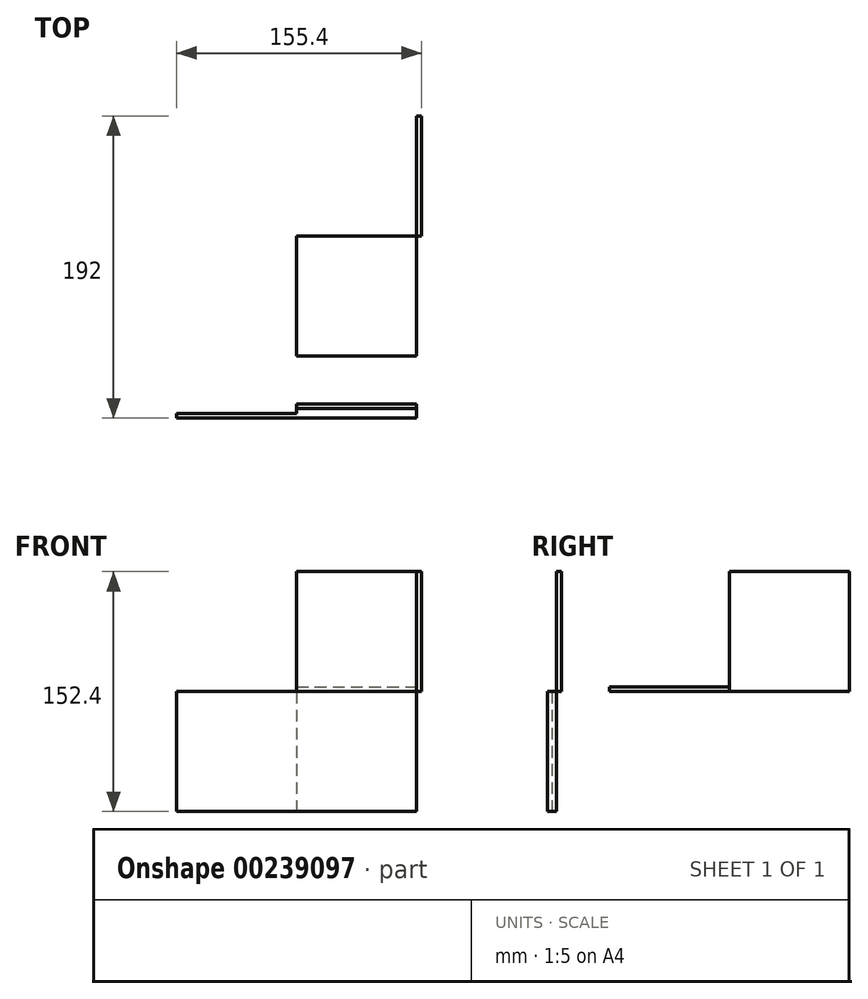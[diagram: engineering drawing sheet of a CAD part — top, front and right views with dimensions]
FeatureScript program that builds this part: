
annotation { "Feature Type Name" : "Feature", "Feature Type Description" : "" }
export const myFeature = defineFeature(function(context is Context, id is Id, definition is map)
    precondition{}
    {
        {
            assignVariable(context, id + "F0", {"name" : "v", "anyValue" : 3});
        }
        {
            var Q0;
            Q0=qCreatedBy(makeId("Front.planeOp"),FACE);
            var sketch = newSketch(context, id + "F1", { "sketchPlane" : qUnion([Q0])});
            skLineSegment(sketch, "E0.bottom", {"start": v(-76.2, 38.1) * mm, "end": v(76.2, 38.1) * mm});
            skLineSegment(sketch, "E0.top", {"start": v(-76.2, -38.1) * mm, "end": v(76.2, -38.1) * mm});
            skLineSegment(sketch, "E0.left", {"start": v(-76.2, 38.1) * mm, "end": v(-76.2, -38.1) * mm});
            skLineSegment(sketch, "E0.right", {"start": v(76.2, 38.1) * mm, "end": v(76.2, -38.1) * mm});
            skPoint(sketch, "E0.middle", {"position": v(0, 0) * mm});
            skSolve(sketch);
        }
        {
            var Q0;
            Q0 = qSketchRegion(id + "F1", true);
            extrude(context, id + "F2", {"entities" : qUnion([Q0]), "endBound" : BoundingType.SYMMETRIC, "depth" : (getVariable(context, 'v')) * mm});
        }
        {
            var Q0;
            Q0=makeQuery(id+"F2.opExtrude","CAP_FACE",FACE,{"disambiguationData":[OSD([sQuery(id+"F1.wireOp",EDGE,"E0.bottom"),sQuery(id+"F1.wireOp",EDGE,"E0.top"),sQuery(id+"F1.wireOp",EDGE,"E0.left"),sQuery(id+"F1.wireOp",EDGE,"E0.right")])],"isStart":true});
            var sketch = newSketch(context, id + "F3", { "sketchPlane" : qUnion([Q0])});
            skLineSegment(sketch, "E1.bottom", {"start": v(-76.2, 38.1) * mm, "end": v(0, 38.1) * mm});
            skLineSegment(sketch, "E1.top", {"start": v(-76.2, -38.1) * mm, "end": v(0, -38.1) * mm});
            skLineSegment(sketch, "E1.left", {"start": v(-76.2, 38.1) * mm, "end": v(-76.2, -38.1) * mm});
            skLineSegment(sketch, "E1.right", {"start": v(0, 38.1) * mm, "end": v(0, -38.1) * mm});
            skSolve(sketch);
        }
        {
            var Q0;
            Q0 = qSketchRegion(id + "F3", true);
            extrude(context, id + "F4", {"entities" : qUnion([Q0]), "operationType" : NewBodyOperationType.ADD, "depth" : (getVariable(context, 'v')) * mm});
        }
        {
            var Q0;
            Q0=makeQuery(id+"F4.boolean.opBoolean","MERGE",FACE,{"derivedFrom":[makeQuery(id+"F2.opExtrude","SWEPT_FACE",FACE,{"disambiguationData":[OSD([sQuery(id+"F1.wireOp",EDGE,"E0.bottom")])]}),makeQuery(id+"F4.opExtrude","SWEPT_FACE",FACE,{"disambiguationData":[OSD([sQuery(id+"F3.wireOp",EDGE,"E1.bottom")])]})]});
            var sketch = newSketch(context, id + "F5", { "sketchPlane" : qUnion([Q0])});
            skLineSegment(sketch, "E2.bottom", {"start": v(0, 114.3) * mm, "end": v(76.2, 114.3) * mm});
            skLineSegment(sketch, "E2.top", {"start": v(0, 38.1) * mm, "end": v(76.2, 38.1) * mm});
            skLineSegment(sketch, "E2.left", {"start": v(0, 114.3) * mm, "end": v(0, 38.1) * mm});
            skLineSegment(sketch, "E2.right", {"start": v(76.2, 114.3) * mm, "end": v(76.2, 38.1) * mm});
            skSolve(sketch);
        }
        {
            var Q0;
            Q0 = qSketchRegion(id + "F5", true);
            extrude(context, id + "F6", {"entities" : qUnion([Q0]), "operationType" : NewBodyOperationType.ADD, "depth" : (getVariable(context, 'v')) * mm});
        }
        {
            var Q0;
            Q0=makeQuery(id+"F6.boolean.opBoolean","MERGE",FACE,{"derivedFrom":[makeQuery(id+"F4.opExtrude","CAP_FACE",FACE,{"disambiguationData":[OSD([sQuery(id+"F3.wireOp",EDGE,"E1.bottom"),sQuery(id+"F3.wireOp",EDGE,"E1.top"),sQuery(id+"F3.wireOp",EDGE,"E1.left"),sQuery(id+"F3.wireOp",EDGE,"E1.right")])],"isStart":false}),makeQuery(id+"F6.opExtrude","SWEPT_FACE",FACE,{"disambiguationData":[OSD([sQuery(id+"F5.wireOp",EDGE,"E2.bottom")])]})]});
            var sketch = newSketch(context, id + "F7", { "sketchPlane" : qUnion([Q0])});
            skLineSegment(sketch, "E3.bottom", {"start": v(-76.2, 114.3) * mm, "end": v(0, 114.3) * mm});
            skLineSegment(sketch, "E3.top", {"start": v(-76.2, 38.1) * mm, "end": v(0, 38.1) * mm});
            skLineSegment(sketch, "E3.left", {"start": v(-76.2, 114.3) * mm, "end": v(-76.2, 38.1) * mm});
            skLineSegment(sketch, "E3.right", {"start": v(0, 114.3) * mm, "end": v(0, 38.1) * mm});
            skSolve(sketch);
        }
        {
            var Q0;
            Q0 = qSketchRegion(id + "F7", true);
            extrude(context, id + "F8", {"entities" : qUnion([Q0]), "operationType" : NewBodyOperationType.ADD, "depth" : (getVariable(context, 'v')) * mm});
        }
        {
            var Q0;
            Q0=makeQuery(id+"F8.boolean.opBoolean","MERGE",FACE,{"derivedFrom":[makeQuery(id+"F6.boolean.opBoolean","MERGE",FACE,{"derivedFrom":[makeQuery(id+"F4.boolean.opBoolean","MERGE",FACE,{"derivedFrom":[makeQuery(id+"F2.opExtrude","SWEPT_FACE",FACE,{"disambiguationData":[OSD([sQuery(id+"F1.wireOp",EDGE,"E0.right")])]}),makeQuery(id+"F4.opExtrude","SWEPT_FACE",FACE,{"disambiguationData":[OSD([sQuery(id+"F3.wireOp",EDGE,"E1.left")])]})]}),makeQuery(id+"F6.opExtrude","SWEPT_FACE",FACE,{"disambiguationData":[OSD([sQuery(id+"F5.wireOp",EDGE,"E2.right")])]})]}),makeQuery(id+"F8.opExtrude","SWEPT_FACE",FACE,{"disambiguationData":[OSD([sQuery(id+"F7.wireOp",EDGE,"E3.left")])]})]});
            var sketch = newSketch(context, id + "F9", { "sketchPlane" : qUnion([Q0])});
            skLineSegment(sketch, "E4.bottom", {"start": v(190.5, 38.1) * mm, "end": v(114.3, 38.1) * mm});
            skLineSegment(sketch, "E4.top", {"start": v(190.5, 114.3) * mm, "end": v(114.3, 114.3) * mm});
            skLineSegment(sketch, "E4.left", {"start": v(190.5, 38.1) * mm, "end": v(190.5, 114.3) * mm});
            skLineSegment(sketch, "E4.right", {"start": v(114.3, 38.1) * mm, "end": v(114.3, 114.3) * mm});
            skSolve(sketch);
        }
        {
            var Q0;
            Q0 = qSketchRegion(id + "F9", true);
            extrude(context, id + "F10", {"entities" : qUnion([Q0]), "operationType" : NewBodyOperationType.ADD, "depth" : (getVariable(context, 'v')) * mm});
        }
    });
